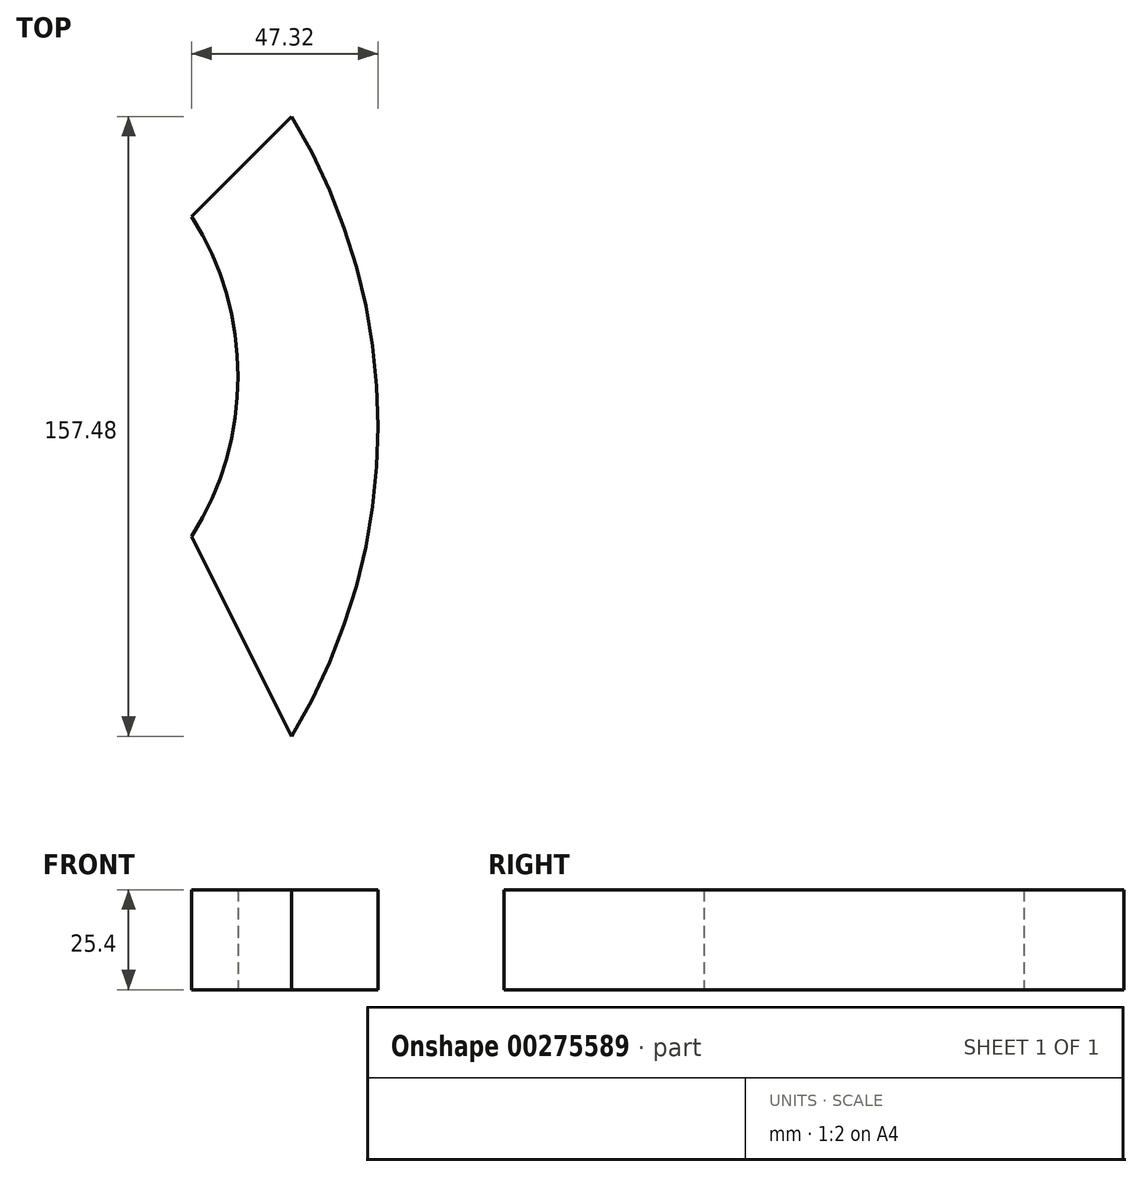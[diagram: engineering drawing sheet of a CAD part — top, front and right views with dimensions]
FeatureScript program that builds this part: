
annotation { "Feature Type Name" : "Feature", "Feature Type Description" : "" }
export const myFeature = defineFeature(function(context is Context, id is Id, definition is map)
    precondition{}
    {
        {
            var Q0;
            Q0=qCreatedBy(makeId("Top.planeOp"),FACE);
            var sketch = newSketch(context, id + "F0", { "sketchPlane" : qUnion([Q0])});
            skLineSegment(sketch, "E0", {"start": v(50.05, 0) * mm, "end": v(50.05, 81.28) * mm});
            skLineSegment(sketch, "E1", {"start": v(50.05, 0) * mm, "end": v(75.45, 0) * mm});
            skLineSegment(sketch, "E2", {"start": v(75.45, 0) * mm, "end": v(75.45, -50.8) * mm});
            skLineSegment(sketch, "E3", {"start": v(75.45, -50.8) * mm, "end": v(75.45, 106.68) * mm});
            skLineSegment(sketch, "E4", {"start": v(75.45, -50.8) * mm, "end": v(75.45, 0) * mm});
            skLineSegment(sketch, "E5", {"start": v(50.05, 0) * mm, "end": v(75.45, -50.8) * mm});
            skLineSegment(sketch, "E6", {"start": v(50.05, 81.28) * mm, "end": v(75.45, 106.68) * mm});
            skArc(sketch, "E7", {"start": v(75.45, -50.8) * mm, "mid": v(97.37, 27.94) * mm, "end": v(75.45, 106.68) * mm});
            skLineSegment(sketch, "E8", {"start": v(50.05, 0) * mm, "end": v(50.05, -25.4) * mm});
            skArc(sketch, "E9", {"start": v(50.05, 0) * mm, "mid": v(61.8, 40.64) * mm, "end": v(50.05, 81.28) * mm});
            skSolve(sketch);
        }
        {
            var Q0;
            Q0=makeQuery(id+"F0.imprint","IMPRINT",FACE,{"disambiguationData":[TD([[makeQuery(id+"F0.imprint","IMPRINT",EDGE,{"derivedFrom":sQuery(id+"F0.wireOp",EDGE,"E1")}),-1.0]])]});
            var Q1;
            Q1=makeQuery(id+"F0.imprint","IMPRINT",FACE,{"disambiguationData":[TD([[makeQuery(id+"F0.imprint","IMPRINT",EDGE,{"derivedFrom":sQuery(id+"F0.wireOp",EDGE,"E3")}),-1.0]])]});
            var Q2;
            Q2=makeQuery(id+"F0.imprint","IMPRINT",FACE,{"disambiguationData":[TD([[makeQuery(id+"F0.imprint","IMPRINT",EDGE,{"derivedFrom":sQuery(id+"F0.wireOp",EDGE,"E1")}),1.0]])]});
            extrude(context, id + "F1", {"entities" : qUnion([Q0, Q1, Q2]), "depth" : 25.4 * mm});
        }
    });
